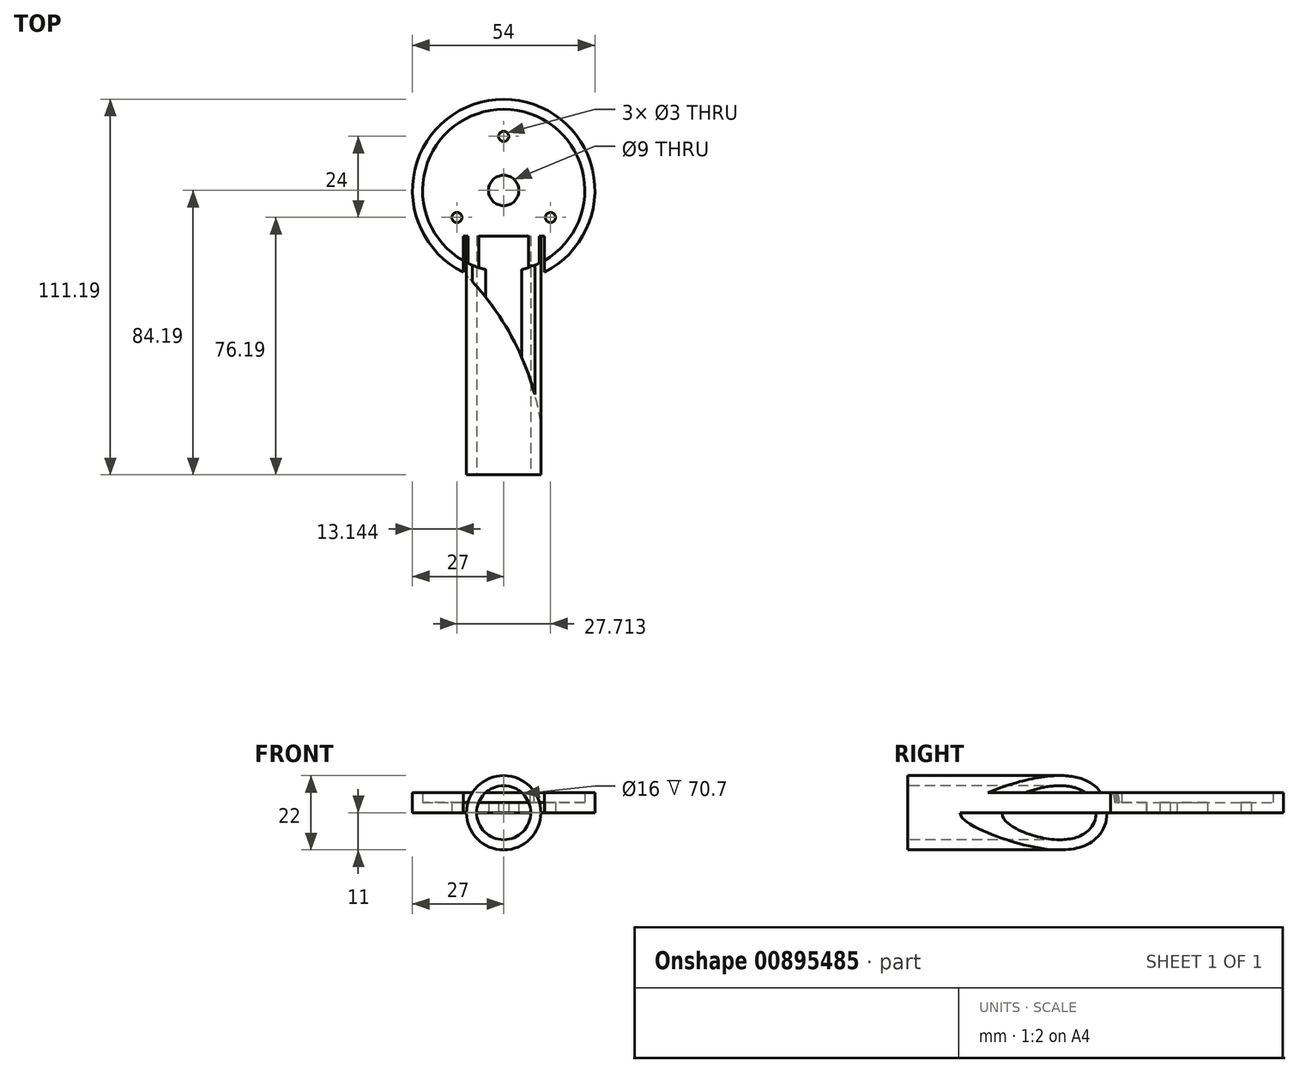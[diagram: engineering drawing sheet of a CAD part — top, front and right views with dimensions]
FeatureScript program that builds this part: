
annotation { "Feature Type Name" : "Feature", "Feature Type Description" : "" }
export const myFeature = defineFeature(function(context is Context, id is Id, definition is map)
    precondition{}
    {
        {
            var Q0;
            Q0=qCreatedBy(makeId("Top.planeOp"),FACE);
            var sketch = newSketch(context, id + "F0", { "sketchPlane" : qUnion([Q0])});
            skCircle(sketch, "E0", {"center": v(0, 0) * mm, "radius": 16 * mm, "construction": true});
            skCircle(sketch, "E1", {"center": v(0, 0) * mm, "radius": 24 * mm});
            skCircle(sketch, "E2", {"center": v(0, 0) * mm, "radius": 4.5 * mm});
            skCircle(sketch, "E3", {"center": v(0, 16) * mm, "radius": 1.5 * mm});
            skCircle(sketch, "E4.1.0", {"center": v(-13.86, -8) * mm, "radius": 1.5 * mm});
            skCircle(sketch, "E4.2.0", {"center": v(13.86, -8) * mm, "radius": 1.5 * mm});
            skLineSegment(sketch, "E5", {"start": v(0, -24) * mm, "end": v(4, -24) * mm, "construction": true});
            skLineSegment(sketch, "E6", {"start": v(4, -24) * mm, "end": v(4, -20) * mm, "construction": true});
            skLineSegment(sketch, "E7.MirrorCS", {"start": v(-4, -24) * mm, "end": v(-4, -20) * mm, "construction": true});
            skLineSegment(sketch, "E8", {"start": v(-4, -20) * mm, "end": v(4, -20) * mm, "construction": true});
            skPoint(sketch, "E9.orphan", {"position": v(8, -24) * mm});
            skCircle(sketch, "E10.0", {"center": v(0, 0) * mm, "radius": 27 * mm});
            skLineSegment(sketch, "E11.bottom", {"start": v(8, -75) * mm, "end": v(-8, -75) * mm, "construction": true});
            skLineSegment(sketch, "E11.top", {"start": v(8, 75) * mm, "end": v(-8, 75) * mm, "construction": true});
            skLineSegment(sketch, "E11.left", {"start": v(8, -75) * mm, "end": v(8, 75) * mm, "construction": true});
            skLineSegment(sketch, "E11.right", {"start": v(-8, -75) * mm, "end": v(-8, 75) * mm, "construction": true});
            skLineSegment(sketch, "E12.0", {"start": v(12, -84.19) * mm, "end": v(12, -24.19) * mm});
            skLineSegment(sketch, "E13.MirrorCS", {"start": v(-12, -84.19) * mm, "end": v(-12, -24.19) * mm});
            skPoint(sketch, "E14.orphan", {"position": v(-12, 75) * mm});
            skPoint(sketch, "E15.orphan", {"position": v(12, 75) * mm});
            skLineSegment(sketch, "E16", {"start": v(-12, -84.19) * mm, "end": v(12, -84.19) * mm});
            skSolve(sketch);
        }
        {
            var Q0;
            Q0=makeQuery(id+"F0.imprint","IMPRINT",FACE,{"disambiguationData":[TD([[makeQuery(id+"F0.imprint","IMPRINT",EDGE,{"derivedFrom":sQuery(id+"F0.wireOp",EDGE,"E1")}),1.0]])]});
            extrude(context, id + "F1", {"entities" : qUnion([Q0]), "depth" : 3 * mm, "offsetDistance" : 25 * mm});
        }
        {
            var Q0;
            Q0=makeQuery(id+"F0.imprint","IMPRINT",FACE,{"disambiguationData":[TD([[makeQuery(id+"F0.imprint","IMPRINT",EDGE,{"derivedFrom":sQuery(id+"F0.wireOp",EDGE,"E1")}),-1.0]])]});
            extrude(context, id + "F2", {"entities" : qUnion([Q0]), "operationType" : NewBodyOperationType.ADD, "depth" : 6 * mm, "offsetDistance" : 25 * mm});
        }
        {
            var Q0;
            {var subQ0=sQuery(id+"F0.wireOp",EDGE,"E12.0");Q0=makeQuery(id+"F0.imprint","IMPRINT",FACE,{"disambiguationData":[TD([[makeQuery(id+"F0.imprint","IMPRINT",EDGE,{"derivedFrom":subQ0}),1.0]])]});}
            var Q1;
            Q1=makeQuery(id+"F2.opExtrude","CAP_FACE",FACE,{"disambiguationData":[OSD([sQuery(id+"F0.wireOp",EDGE,"E1"),sQuery(id+"F0.wireOp",EDGE,"E10.0")])],"isStart":false});
            extrude(context, id + "F3", {"entities" : qUnion([Q0]), "operationType" : NewBodyOperationType.ADD, "depth" : 24.8 * mm, "endBoundEntityFace" : qUnion([Q1]), "offsetDistance" : 25 * mm, "symmetric" : true});
        }
        {
            var Q0;
            {var subQ0=sQuery(id+"F0.wireOp",EDGE,"E10.0");var subQ1=sQuery(id+"F0.wireOp",EDGE,"E12.0");Q0=makeQuery(id+"F3.boolean.opBoolean","SPLIT",EDGE,{"disambiguationData":[topologyDisambiguationEdgeConnected([makeQuery(id+"F2.opExtrude","SWEPT_FACE",FACE,{"disambiguationData":[OSD([subQ0])]}),makeQuery(id+"F3.opExtrude","SWEPT_FACE",FACE,{"disambiguationData":[OSD([subQ1])]})])],"derivedFrom":makeQuery(id+"F3.opExtrude","SWEPT_EDGE",EDGE,{"disambiguationData":[OSD([subQ0,subQ1])]})});}
            fillet(context, id + "F4", {"entities" : qUnion([Q0]), "radius" : 80 * mm, "tangentPropagation" : true, "allowEdgeOverflow" : false});
        }
        {
            var Q0;
            Q0=makeQuery(id+"F3.opExtrude","SWEPT_FACE",FACE,{"disambiguationData":[OSD([sQuery(id+"F0.wireOp",EDGE,"E16")])]});
            var sketch = newSketch(context, id + "F5", { "sketchPlane" : qUnion([Q0])});
            skCircle(sketch, "E17", {"center": v(0, 0) * mm, "radius": 8 * mm});
            skCircle(sketch, "E18.0", {"center": v(0, 0) * mm, "radius": 11 * mm});
            skSolve(sketch);
        }
        {
            var Q0;
            Q0=makeQuery(id+"F5.imprint","IMPRINT",FACE,{"disambiguationData":[TD([[makeQuery(id+"F5.imprint","IMPRINT",EDGE,{"derivedFrom":sQuery(id+"F5.wireOp",EDGE,"E18.0")}),-1.0]])]});
            var Q1;
            Q1=makeQuery(id+"F5.imprint","IMPRINT",FACE,{"disambiguationData":[TD([[makeQuery(id+"F5.imprint","IMPRINT",EDGE,{"derivedFrom":sQuery(id+"F5.wireOp",EDGE,"E17")}),1.0]])]});
            extrude(context, id + "F6", {"entities" : qUnion([Q0, Q1]), "operationType" : NewBodyOperationType.REMOVE, "oppositeDirection" : true, "depth" : 61.9 * mm, "offsetDistance" : 25 * mm});
        }
        {
            var Q0;
            Q0=makeQuery(id+"F6.boolean.opBoolean","COPY",FACE,{"derivedFrom":makeQuery(id+"F6.opExtrude","SWEPT_FACE",FACE,{"disambiguationData":[OSD([sQuery(id+"F0.wireOp",EDGE,"E12.0"),sQuery(id+"F0.wireOp",EDGE,"E16")])]})});
            var sketch = newSketch(context, id + "F7", { "sketchPlane" : qUnion([Q0])});
            skLineSegment(sketch, "E19.0", {"start": v(54.64, 6) * mm, "end": v(22.29, 6) * mm});
            skLineSegment(sketch, "E19.1", {"start": v(54.64, 0) * mm, "end": v(54.64, 6) * mm});
            skLineSegment(sketch, "E19.2", {"start": v(22.29, 3) * mm, "end": v(22.29, 6) * mm});
            skLineSegment(sketch, "E19.4", {"start": v(84.19, 0) * mm, "end": v(24.19, 0) * mm});
            skLineSegment(sketch, "E20", {"start": v(24.19, 0) * mm, "end": v(22.29, 0) * mm});
            skLineSegment(sketch, "E21", {"start": v(22.29, 0) * mm, "end": v(22.29, 3) * mm});
            skSolve(sketch);
        }
        {
            var Q0;
            Q0 = qSketchRegion(id + "F7", true);
            extrude(context, id + "F8", {"entities" : qUnion([Q0]), "operationType" : NewBodyOperationType.ADD, "depth" : 4.2 * mm, "offsetDistance" : 25 * mm});
        }
        {
            var Q0;
            Q0=makeQuery(id+"F8.boolean.opBoolean","INTERSECT",EDGE,{"derivedFrom":[makeQuery(id+"F6.boolean.opBoolean","COPY",FACE,{"derivedFrom":makeQuery(id+"F6.opExtrude","SWEPT_FACE",FACE,{"disambiguationData":[OSD([sQuery(id+"F5.wireOp",EDGE,"E18.0")])]})}),makeQuery(id+"F8.opExtrude","SWEPT_FACE",FACE,{"disambiguationData":[OSD([sQuery(id+"F7.wireOp",EDGE,"E19.0")])]})]});
            var Q1;
            Q1=makeQuery(id+"F8.boolean.opBoolean","INTERSECT",EDGE,{"derivedFrom":[makeQuery(id+"F6.boolean.opBoolean","COPY",FACE,{"derivedFrom":makeQuery(id+"F6.opExtrude","SWEPT_FACE",FACE,{"disambiguationData":[OSD([sQuery(id+"F5.wireOp",EDGE,"E18.0")])]})}),makeQuery(id+"F8.opExtrude","SWEPT_FACE",FACE,{"disambiguationData":[OSD([sQuery(id+"F7.wireOp",EDGE,"E19.1")])]})]});
            var Q2;
            Q2=makeQuery(id+"F8.boolean.opBoolean","INTERSECT",EDGE,{"derivedFrom":[makeQuery(id+"F6.boolean.opBoolean","COPY",FACE,{"derivedFrom":makeQuery(id+"F6.opExtrude","SWEPT_FACE",FACE,{"disambiguationData":[OSD([sQuery(id+"F5.wireOp",EDGE,"E18.0")])]})}),makeQuery(id+"F8.opExtrude","SWEPT_FACE",FACE,{"disambiguationData":[OSD([sQuery(id+"F7.wireOp",EDGE,"E19.4"),sQuery(id+"F7.wireOp",EDGE,"E20")])]})]});
            fillet(context, id + "F9", {"entities" : qUnion([Q0, Q1, Q2]), "radius" : 2 * mm, "tangentPropagation" : true, "allowEdgeOverflow" : false});
        }
        {
            var Q0;
            {var subQ0=sQuery(id+"F0.wireOp",EDGE,"E16");Q0=makeQuery(id+"F5.imprint","IMPRINT",FACE,{"disambiguationData":[TD([[makeQuery(id+"F5.imprint","IMPRINT",EDGE,{"derivedFrom":makeQuery(id+"F3.opExtrude","CAP_EDGE",EDGE,{"disambiguationData":[OSD([subQ0])],"isStart":false})}),-1.0]])]});}
            var Q1;
            {var subQ0=sQuery(id+"F5.wireOp",EDGE,"E17");var subQ1=makeQuery(id+"F3.opExtrude","CAP_EDGE",EDGE,{"disambiguationData":[OSD([sQuery(id+"F0.wireOp",EDGE,"E16")])],"isStart":true});var subQ2=makeQuery(id+"F5.imprint","INTERSECT",VERTEX,{"disambiguationData":[OD(0.0)],"derivedFrom":[subQ1,subQ0]});Q1=makeQuery(id+"F5.imprint","IMPRINT",FACE,{"disambiguationData":[TD([[makeQuery(id+"F5.imprint","IMPRINT",EDGE,{"disambiguationData":[TD([[subQ2,-1.0]])],"derivedFrom":subQ0}),1.0]])]});}
            extrude(context, id + "F10", {"entities" : qUnion([Q0, Q1]), "operationType" : NewBodyOperationType.REMOVE, "oppositeDirection" : true, "depth" : 70.7 * mm, "offsetDistance" : 25 * mm});
        }
    });
